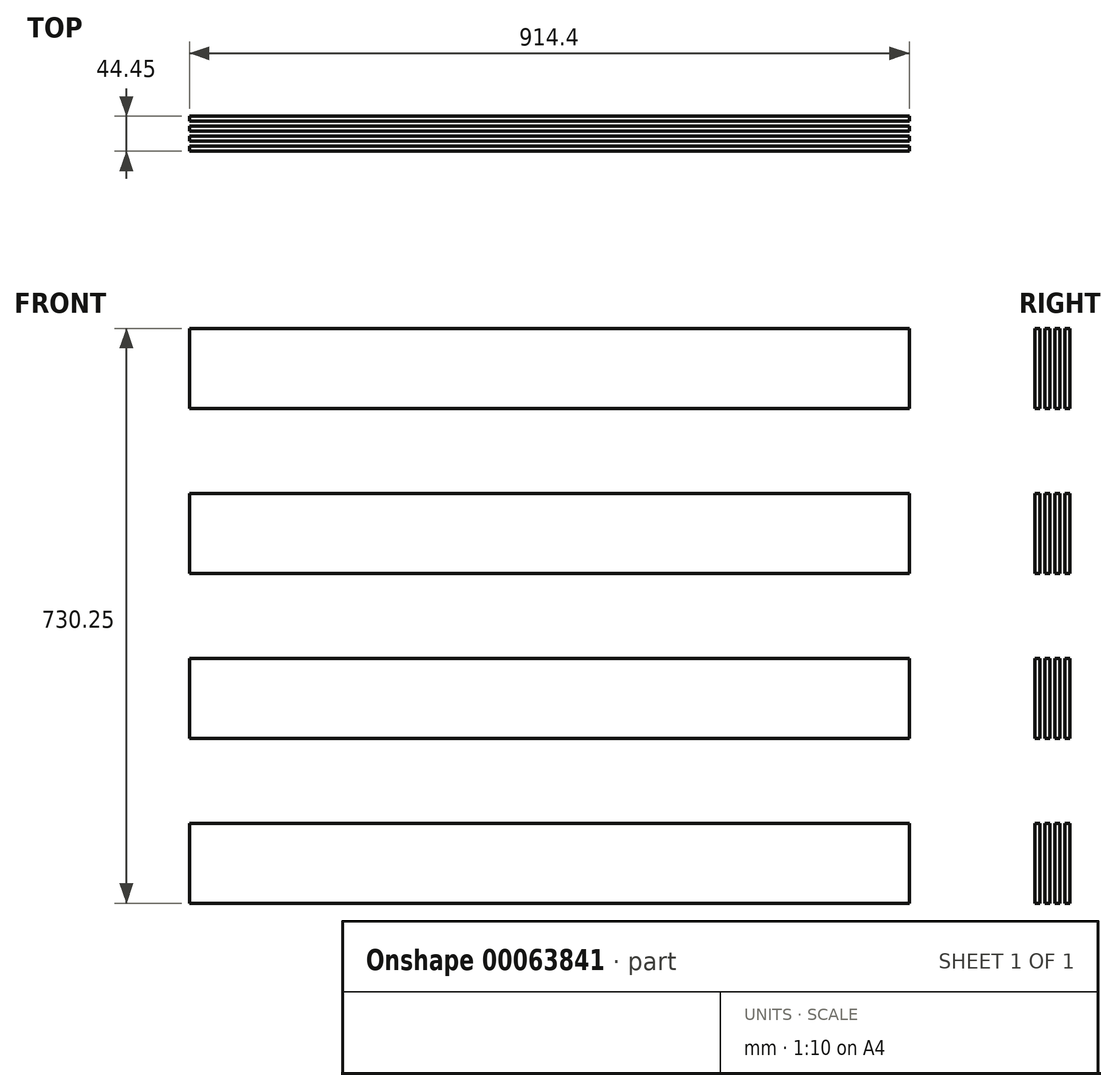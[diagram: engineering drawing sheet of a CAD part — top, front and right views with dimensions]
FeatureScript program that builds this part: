
annotation { "Feature Type Name" : "Feature", "Feature Type Description" : "" }
export const myFeature = defineFeature(function(context is Context, id is Id, definition is map)
    precondition{}
    {
        {
            var Q0;
            Q0=qCreatedBy(makeId("Right.planeOp"),FACE);
            var sketch = newSketch(context, id + "F0", { "sketchPlane" : qUnion([Q0])});
            skLineSegment(sketch, "E0.bottom", {"start": v(0, 0) * mm, "end": v(6.35, 0) * mm});
            skLineSegment(sketch, "E0.top", {"start": v(0, 101.6) * mm, "end": v(6.35, 101.6) * mm});
            skLineSegment(sketch, "E0.left", {"start": v(0, 0) * mm, "end": v(0, 101.6) * mm});
            skLineSegment(sketch, "E0.right", {"start": v(6.35, 0) * mm, "end": v(6.35, 101.6) * mm});
            skLineSegment(sketch, "E1.0.1.0", {"start": v(0, -209.55) * mm, "end": v(0, -107.95) * mm});
            skLineSegment(sketch, "E1.0.1.1", {"start": v(6.35, -209.55) * mm, "end": v(6.35, -107.95) * mm});
            skLineSegment(sketch, "E1.0.1.2", {"start": v(0, -107.95) * mm, "end": v(6.35, -107.95) * mm});
            skLineSegment(sketch, "E1.0.1.3", {"start": v(0, -209.55) * mm, "end": v(6.35, -209.55) * mm});
            skLineSegment(sketch, "E1.0.2.0", {"start": v(0, -419.1) * mm, "end": v(0, -317.5) * mm});
            skLineSegment(sketch, "E1.0.2.1", {"start": v(6.35, -419.1) * mm, "end": v(6.35, -317.5) * mm});
            skLineSegment(sketch, "E1.0.2.2", {"start": v(0, -317.5) * mm, "end": v(6.35, -317.5) * mm});
            skLineSegment(sketch, "E1.0.2.3", {"start": v(0, -419.1) * mm, "end": v(6.35, -419.1) * mm});
            skLineSegment(sketch, "E1.0.3.0", {"start": v(0, -628.65) * mm, "end": v(0, -527.05) * mm});
            skLineSegment(sketch, "E1.0.3.1", {"start": v(6.35, -628.65) * mm, "end": v(6.35, -527.05) * mm});
            skLineSegment(sketch, "E1.0.3.2", {"start": v(0, -527.05) * mm, "end": v(6.35, -527.05) * mm});
            skLineSegment(sketch, "E1.0.3.3", {"start": v(0, -628.65) * mm, "end": v(6.35, -628.65) * mm});
            skLineSegment(sketch, "E1.1.0.0", {"start": v(12.7, 0) * mm, "end": v(12.7, 101.6) * mm});
            skLineSegment(sketch, "E1.1.0.1", {"start": v(19.05, 0) * mm, "end": v(19.05, 101.6) * mm});
            skLineSegment(sketch, "E1.1.0.2", {"start": v(12.7, 101.6) * mm, "end": v(19.05, 101.6) * mm});
            skLineSegment(sketch, "E1.1.0.3", {"start": v(12.7, 0) * mm, "end": v(19.05, 0) * mm});
            skLineSegment(sketch, "E1.1.1.0", {"start": v(12.7, -209.55) * mm, "end": v(12.7, -107.95) * mm});
            skLineSegment(sketch, "E1.1.1.1", {"start": v(19.05, -209.55) * mm, "end": v(19.05, -107.95) * mm});
            skLineSegment(sketch, "E1.1.1.2", {"start": v(12.7, -107.95) * mm, "end": v(19.05, -107.95) * mm});
            skLineSegment(sketch, "E1.1.1.3", {"start": v(12.7, -209.55) * mm, "end": v(19.05, -209.55) * mm});
            skLineSegment(sketch, "E1.1.2.0", {"start": v(12.7, -419.1) * mm, "end": v(12.7, -317.5) * mm});
            skLineSegment(sketch, "E1.1.2.1", {"start": v(19.05, -419.1) * mm, "end": v(19.05, -317.5) * mm});
            skLineSegment(sketch, "E1.1.2.2", {"start": v(12.7, -317.5) * mm, "end": v(19.05, -317.5) * mm});
            skLineSegment(sketch, "E1.1.2.3", {"start": v(12.7, -419.1) * mm, "end": v(19.05, -419.1) * mm});
            skLineSegment(sketch, "E1.1.3.0", {"start": v(12.7, -628.65) * mm, "end": v(12.7, -527.05) * mm});
            skLineSegment(sketch, "E1.1.3.1", {"start": v(19.05, -628.65) * mm, "end": v(19.05, -527.05) * mm});
            skLineSegment(sketch, "E1.1.3.2", {"start": v(12.7, -527.05) * mm, "end": v(19.05, -527.05) * mm});
            skLineSegment(sketch, "E1.1.3.3", {"start": v(12.7, -628.65) * mm, "end": v(19.05, -628.65) * mm});
            skLineSegment(sketch, "E1.2.0.0", {"start": v(25.4, 0) * mm, "end": v(25.4, 101.6) * mm});
            skLineSegment(sketch, "E1.2.0.1", {"start": v(31.75, 0) * mm, "end": v(31.75, 101.6) * mm});
            skLineSegment(sketch, "E1.2.0.2", {"start": v(25.4, 101.6) * mm, "end": v(31.75, 101.6) * mm});
            skLineSegment(sketch, "E1.2.0.3", {"start": v(25.4, 0) * mm, "end": v(31.75, 0) * mm});
            skLineSegment(sketch, "E1.2.1.0", {"start": v(25.4, -209.55) * mm, "end": v(25.4, -107.95) * mm});
            skLineSegment(sketch, "E1.2.1.1", {"start": v(31.75, -209.55) * mm, "end": v(31.75, -107.95) * mm});
            skLineSegment(sketch, "E1.2.1.2", {"start": v(25.4, -107.95) * mm, "end": v(31.75, -107.95) * mm});
            skLineSegment(sketch, "E1.2.1.3", {"start": v(25.4, -209.55) * mm, "end": v(31.75, -209.55) * mm});
            skLineSegment(sketch, "E1.2.2.0", {"start": v(25.4, -419.1) * mm, "end": v(25.4, -317.5) * mm});
            skLineSegment(sketch, "E1.2.2.1", {"start": v(31.75, -419.1) * mm, "end": v(31.75, -317.5) * mm});
            skLineSegment(sketch, "E1.2.2.2", {"start": v(25.4, -317.5) * mm, "end": v(31.75, -317.5) * mm});
            skLineSegment(sketch, "E1.2.2.3", {"start": v(25.4, -419.1) * mm, "end": v(31.75, -419.1) * mm});
            skLineSegment(sketch, "E1.2.3.0", {"start": v(25.4, -628.65) * mm, "end": v(25.4, -527.05) * mm});
            skLineSegment(sketch, "E1.2.3.1", {"start": v(31.75, -628.65) * mm, "end": v(31.75, -527.05) * mm});
            skLineSegment(sketch, "E1.2.3.2", {"start": v(25.4, -527.05) * mm, "end": v(31.75, -527.05) * mm});
            skLineSegment(sketch, "E1.2.3.3", {"start": v(25.4, -628.65) * mm, "end": v(31.75, -628.65) * mm});
            skLineSegment(sketch, "E1.3.0.0", {"start": v(38.1, 0) * mm, "end": v(38.1, 101.6) * mm});
            skLineSegment(sketch, "E1.3.0.1", {"start": v(44.45, 0) * mm, "end": v(44.45, 101.6) * mm});
            skLineSegment(sketch, "E1.3.0.2", {"start": v(38.1, 101.6) * mm, "end": v(44.45, 101.6) * mm});
            skLineSegment(sketch, "E1.3.0.3", {"start": v(38.1, 0) * mm, "end": v(44.45, 0) * mm});
            skLineSegment(sketch, "E1.3.1.0", {"start": v(38.1, -209.55) * mm, "end": v(38.1, -107.95) * mm});
            skLineSegment(sketch, "E1.3.1.1", {"start": v(44.45, -209.55) * mm, "end": v(44.45, -107.95) * mm});
            skLineSegment(sketch, "E1.3.1.2", {"start": v(38.1, -107.95) * mm, "end": v(44.45, -107.95) * mm});
            skLineSegment(sketch, "E1.3.1.3", {"start": v(38.1, -209.55) * mm, "end": v(44.45, -209.55) * mm});
            skLineSegment(sketch, "E1.3.2.0", {"start": v(38.1, -419.1) * mm, "end": v(38.1, -317.5) * mm});
            skLineSegment(sketch, "E1.3.2.1", {"start": v(44.45, -419.1) * mm, "end": v(44.45, -317.5) * mm});
            skLineSegment(sketch, "E1.3.2.2", {"start": v(38.1, -317.5) * mm, "end": v(44.45, -317.5) * mm});
            skLineSegment(sketch, "E1.3.2.3", {"start": v(38.1, -419.1) * mm, "end": v(44.45, -419.1) * mm});
            skLineSegment(sketch, "E1.3.3.0", {"start": v(38.1, -628.65) * mm, "end": v(38.1, -527.05) * mm});
            skLineSegment(sketch, "E1.3.3.1", {"start": v(44.45, -628.65) * mm, "end": v(44.45, -527.05) * mm});
            skLineSegment(sketch, "E1.3.3.2", {"start": v(38.1, -527.05) * mm, "end": v(44.45, -527.05) * mm});
            skLineSegment(sketch, "E1.3.3.3", {"start": v(38.1, -628.65) * mm, "end": v(44.45, -628.65) * mm});
            skLineSegment(sketch, "E1.direction1", {"start": v(0, 0) * mm, "end": v(12.7, 0) * mm, "construction": true});
            skLineSegment(sketch, "E1.direction2", {"start": v(0, 0) * mm, "end": v(0, -209.55) * mm, "construction": true});
            skSolve(sketch);
        }
        {
            var Q0;
            Q0 = qSketchRegion(id + "F0", true);
            extrude(context, id + "F1", {"entities" : qUnion([Q0]), "endBound" : BoundingType.SYMMETRIC, "depth" : 914.4 * mm});
        }
    });
